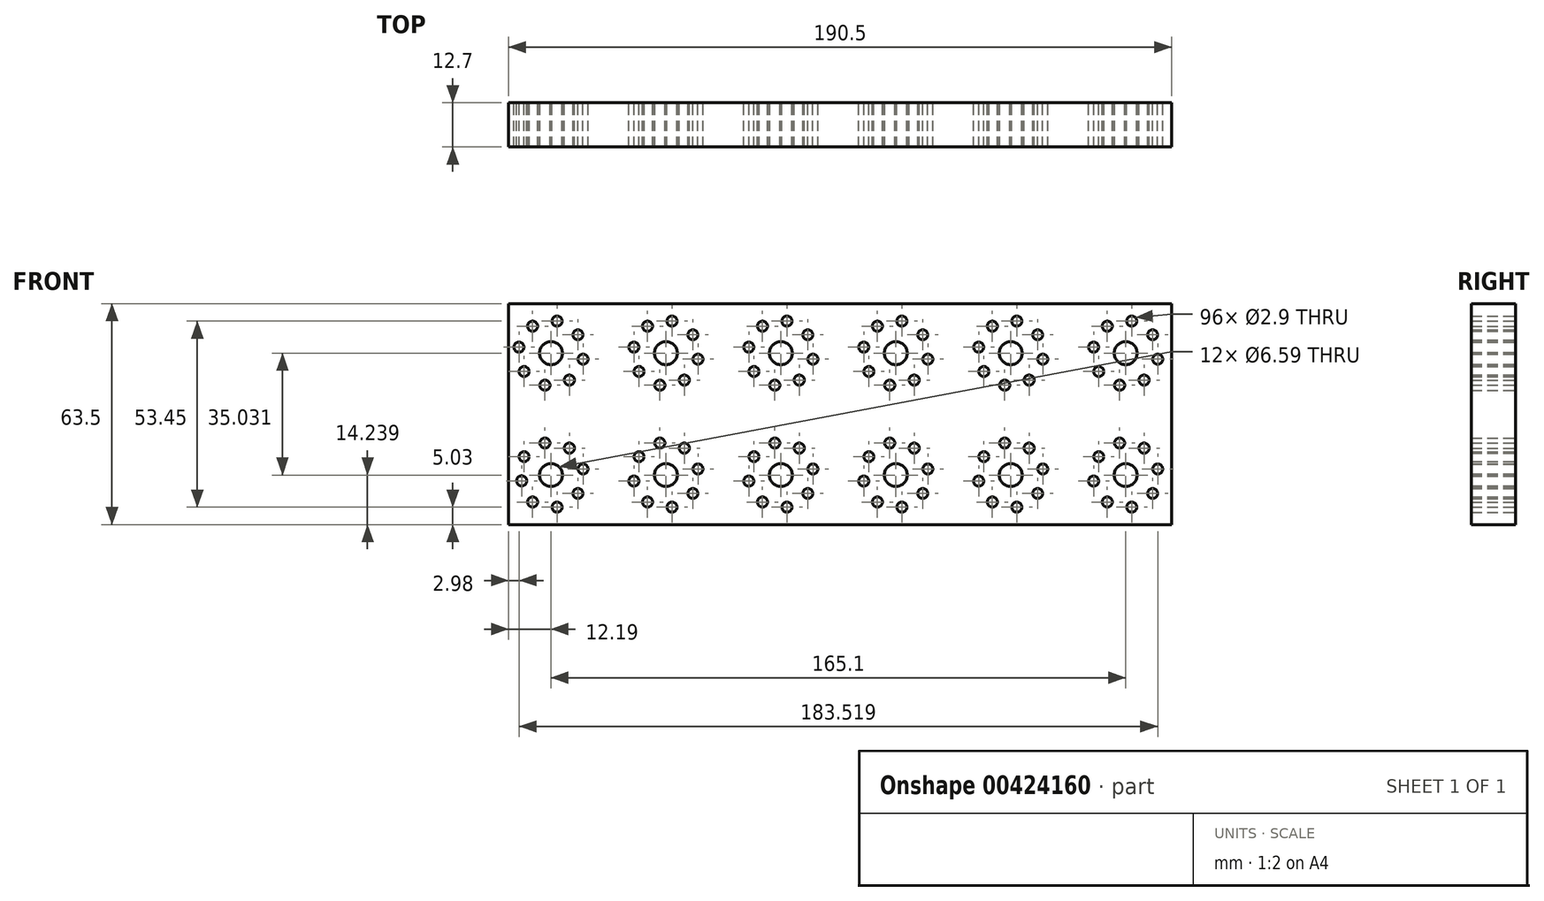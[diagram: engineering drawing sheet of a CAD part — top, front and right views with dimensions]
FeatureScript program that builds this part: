
annotation { "Feature Type Name" : "Feature", "Feature Type Description" : "" }
export const myFeature = defineFeature(function(context is Context, id is Id, definition is map)
    precondition{}
    {
        {
            var Q0;
            Q0=qCreatedBy(makeId("Front.planeOp"),FACE);
            var sketch = newSketch(context, id + "F0", { "sketchPlane" : qUnion([Q0])});
            skPoint(sketch, "E0.middle", {"position": v(0, 0) * mm});
            skCircle(sketch, "E1", {"center": v(-73.12, 32.93) * mm, "radius": 3.3 * mm});
            skCircle(sketch, "E2", {"center": v(-65.38, 38.21) * mm, "radius": 1.45 * mm});
            skCircle(sketch, "E3.1.0", {"center": v(-71.38, 42.14) * mm, "radius": 1.45 * mm});
            skCircle(sketch, "E3.2.0", {"center": v(-78.4, 40.67) * mm, "radius": 1.45 * mm});
            skCircle(sketch, "E3.3.0", {"center": v(-82.33, 34.67) * mm, "radius": 1.45 * mm});
            skCircle(sketch, "E3.4.0", {"center": v(-80.86, 27.65) * mm, "radius": 1.45 * mm});
            skCircle(sketch, "E3.5.0", {"center": v(-74.86, 23.72) * mm, "radius": 1.45 * mm});
            skCircle(sketch, "E3.6.0", {"center": v(-67.84, 25.19) * mm, "radius": 1.45 * mm});
            skCircle(sketch, "E3.7.0", {"center": v(-63.91, 31.2) * mm, "radius": 1.45 * mm});
            skCircle(sketch, "E4.1.0.0", {"center": v(-49.3, 34.67) * mm, "radius": 1.45 * mm});
            skCircle(sketch, "E4.1.0.1", {"center": v(-45.38, 40.67) * mm, "radius": 1.45 * mm});
            skCircle(sketch, "E4.1.0.2", {"center": v(-41.84, 23.72) * mm, "radius": 1.45 * mm});
            skCircle(sketch, "E4.1.0.3", {"center": v(-34.82, 25.19) * mm, "radius": 1.45 * mm});
            skPoint(sketch, "E4.1.0.4", {"position": v(-40.1, 32.93) * mm});
            skCircle(sketch, "E4.1.0.5", {"center": v(-30.9, 31.2) * mm, "radius": 1.45 * mm});
            skCircle(sketch, "E4.1.0.6", {"center": v(-32.36, 38.21) * mm, "radius": 1.45 * mm});
            skCircle(sketch, "E4.1.0.7", {"center": v(-38.36, 42.14) * mm, "radius": 1.45 * mm});
            skCircle(sketch, "E4.1.0.8", {"center": v(-47.84, 27.65) * mm, "radius": 1.45 * mm});
            skCircle(sketch, "E4.1.0.9", {"center": v(-40.1, 32.93) * mm, "radius": 3.3 * mm});
            skCircle(sketch, "E4.2.0.0", {"center": v(-16.29, 34.67) * mm, "radius": 1.45 * mm});
            skCircle(sketch, "E4.2.0.1", {"center": v(-12.36, 40.67) * mm, "radius": 1.45 * mm});
            skCircle(sketch, "E4.2.0.2", {"center": v(-8.82, 23.72) * mm, "radius": 1.45 * mm});
            skCircle(sketch, "E4.2.0.3", {"center": v(-1.8, 25.19) * mm, "radius": 1.45 * mm});
            skPoint(sketch, "E4.2.0.4", {"position": v(-7.08, 32.93) * mm});
            skCircle(sketch, "E4.2.0.5", {"center": v(2.13, 31.2) * mm, "radius": 1.45 * mm});
            skCircle(sketch, "E4.2.0.6", {"center": v(0.66, 38.21) * mm, "radius": 1.45 * mm});
            skCircle(sketch, "E4.2.0.7", {"center": v(-5.34, 42.14) * mm, "radius": 1.45 * mm});
            skCircle(sketch, "E4.2.0.8", {"center": v(-14.82, 27.65) * mm, "radius": 1.45 * mm});
            skCircle(sketch, "E4.2.0.9", {"center": v(-7.08, 32.93) * mm, "radius": 3.3 * mm});
            skCircle(sketch, "E4.3.0.0", {"center": v(16.73, 34.67) * mm, "radius": 1.45 * mm});
            skCircle(sketch, "E4.3.0.1", {"center": v(20.66, 40.67) * mm, "radius": 1.45 * mm});
            skCircle(sketch, "E4.3.0.2", {"center": v(24.2, 23.72) * mm, "radius": 1.45 * mm});
            skCircle(sketch, "E4.3.0.3", {"center": v(31.22, 25.19) * mm, "radius": 1.45 * mm});
            skPoint(sketch, "E4.3.0.4", {"position": v(25.94, 32.93) * mm});
            skCircle(sketch, "E4.3.0.5", {"center": v(35.15, 31.2) * mm, "radius": 1.45 * mm});
            skCircle(sketch, "E4.3.0.6", {"center": v(33.68, 38.21) * mm, "radius": 1.45 * mm});
            skCircle(sketch, "E4.3.0.7", {"center": v(27.68, 42.14) * mm, "radius": 1.45 * mm});
            skCircle(sketch, "E4.3.0.8", {"center": v(18.2, 27.65) * mm, "radius": 1.45 * mm});
            skCircle(sketch, "E4.3.0.9", {"center": v(25.94, 32.93) * mm, "radius": 3.3 * mm});
            skCircle(sketch, "E4.4.0.0", {"center": v(49.75, 34.67) * mm, "radius": 1.45 * mm});
            skCircle(sketch, "E4.4.0.1", {"center": v(53.68, 40.67) * mm, "radius": 1.45 * mm});
            skCircle(sketch, "E4.4.0.2", {"center": v(57.22, 23.72) * mm, "radius": 1.45 * mm});
            skCircle(sketch, "E4.4.0.3", {"center": v(64.24, 25.19) * mm, "radius": 1.45 * mm});
            skPoint(sketch, "E4.4.0.4", {"position": v(58.96, 32.93) * mm});
            skCircle(sketch, "E4.4.0.5", {"center": v(68.17, 31.2) * mm, "radius": 1.45 * mm});
            skCircle(sketch, "E4.4.0.6", {"center": v(66.7, 38.21) * mm, "radius": 1.45 * mm});
            skCircle(sketch, "E4.4.0.7", {"center": v(60.7, 42.14) * mm, "radius": 1.45 * mm});
            skCircle(sketch, "E4.4.0.8", {"center": v(51.22, 27.65) * mm, "radius": 1.45 * mm});
            skCircle(sketch, "E4.4.0.9", {"center": v(58.96, 32.93) * mm, "radius": 3.3 * mm});
            skCircle(sketch, "E4.5.0.0", {"center": v(82.77, 34.67) * mm, "radius": 1.45 * mm});
            skCircle(sketch, "E4.5.0.1", {"center": v(86.7, 40.67) * mm, "radius": 1.45 * mm});
            skCircle(sketch, "E4.5.0.2", {"center": v(90.24, 23.72) * mm, "radius": 1.45 * mm});
            skCircle(sketch, "E4.5.0.3", {"center": v(97.26, 25.19) * mm, "radius": 1.45 * mm});
            skPoint(sketch, "E4.5.0.4", {"position": v(91.98, 32.93) * mm});
            skCircle(sketch, "E4.5.0.5", {"center": v(101.19, 31.2) * mm, "radius": 1.45 * mm});
            skCircle(sketch, "E4.5.0.6", {"center": v(99.72, 38.21) * mm, "radius": 1.45 * mm});
            skCircle(sketch, "E4.5.0.7", {"center": v(93.72, 42.14) * mm, "radius": 1.45 * mm});
            skCircle(sketch, "E4.5.0.8", {"center": v(84.24, 27.65) * mm, "radius": 1.45 * mm});
            skCircle(sketch, "E4.5.0.9", {"center": v(91.98, 32.93) * mm, "radius": 3.3 * mm});
            skLineSegment(sketch, "E4.direction1", {"start": v(-80.86, 27.65) * mm, "end": v(-47.84, 27.65) * mm, "construction": true});
            skLineSegment(sketch, "E5.bottom", {"start": v(-85.3, 47.16) * mm, "end": v(105.2, 47.16) * mm});
            skLineSegment(sketch, "E5.top", {"start": v(-85.3, -16.34) * mm, "end": v(105.2, -16.34) * mm});
            skLineSegment(sketch, "E5.left", {"start": v(-85.3, 47.16) * mm, "end": v(-85.3, -16.34) * mm});
            skLineSegment(sketch, "E5.right", {"start": v(105.2, 47.16) * mm, "end": v(105.2, -16.34) * mm});
            skCircle(sketch, "E6.MirrorC", {"center": v(-80.86, 3.18) * mm, "radius": 1.45 * mm});
            skCircle(sketch, "E7.MirrorC", {"center": v(-47.84, 3.18) * mm, "radius": 1.45 * mm});
            skCircle(sketch, "E8.MirrorC", {"center": v(-8.82, 7.1) * mm, "radius": 1.45 * mm});
            skCircle(sketch, "E9.MirrorC", {"center": v(-71.38, -11.31) * mm, "radius": 1.45 * mm});
            skCircle(sketch, "E10.MirrorC", {"center": v(-65.38, -7.38) * mm, "radius": 1.45 * mm});
            skCircle(sketch, "E11.MirrorC", {"center": v(-78.4, -9.84) * mm, "radius": 1.45 * mm});
            skCircle(sketch, "E12.MirrorC", {"center": v(-49.3, -3.84) * mm, "radius": 1.45 * mm});
            skCircle(sketch, "E13.MirrorC", {"center": v(-45.38, -9.84) * mm, "radius": 1.45 * mm});
            skCircle(sketch, "E14.MirrorC", {"center": v(27.68, -11.31) * mm, "radius": 1.45 * mm});
            skCircle(sketch, "E15.MirrorC", {"center": v(51.22, 3.18) * mm, "radius": 1.45 * mm});
            skCircle(sketch, "E16.MirrorC", {"center": v(35.15, -0.36) * mm, "radius": 1.45 * mm});
            skCircle(sketch, "E17.MirrorC", {"center": v(0.66, -7.38) * mm, "radius": 1.45 * mm});
            skCircle(sketch, "E18.MirrorC", {"center": v(90.24, 7.1) * mm, "radius": 1.45 * mm});
            skCircle(sketch, "E19.MirrorC", {"center": v(57.22, 7.1) * mm, "radius": 1.45 * mm});
            skCircle(sketch, "E20.MirrorC", {"center": v(64.24, 5.64) * mm, "radius": 1.45 * mm});
            skCircle(sketch, "E21.MirrorC", {"center": v(-34.82, 5.64) * mm, "radius": 1.45 * mm});
            skCircle(sketch, "E22.MirrorC", {"center": v(16.73, -3.84) * mm, "radius": 1.45 * mm});
            skCircle(sketch, "E23.MirrorC", {"center": v(2.13, -0.36) * mm, "radius": 1.45 * mm});
            skCircle(sketch, "E24.MirrorC", {"center": v(82.77, -3.84) * mm, "radius": 1.45 * mm});
            skCircle(sketch, "E25.MirrorC", {"center": v(84.24, 3.18) * mm, "radius": 1.45 * mm});
            skCircle(sketch, "E26.MirrorC", {"center": v(-74.86, 7.1) * mm, "radius": 1.45 * mm});
            skCircle(sketch, "E27.MirrorC", {"center": v(24.2, 7.1) * mm, "radius": 1.45 * mm});
            skCircle(sketch, "E28.MirrorC", {"center": v(49.75, -3.84) * mm, "radius": 1.45 * mm});
            skCircle(sketch, "E29.MirrorC", {"center": v(-16.29, -3.84) * mm, "radius": 1.45 * mm});
            skCircle(sketch, "E30.MirrorC", {"center": v(-63.91, -0.36) * mm, "radius": 1.45 * mm});
            skCircle(sketch, "E31.MirrorC", {"center": v(-12.36, -9.84) * mm, "radius": 1.45 * mm});
            skCircle(sketch, "E32.MirrorC", {"center": v(31.22, 5.64) * mm, "radius": 1.45 * mm});
            skCircle(sketch, "E33.MirrorC", {"center": v(-41.84, 7.1) * mm, "radius": 1.45 * mm});
            skCircle(sketch, "E34.MirrorC", {"center": v(53.68, -9.84) * mm, "radius": 1.45 * mm});
            skCircle(sketch, "E35.MirrorC", {"center": v(86.7, -9.84) * mm, "radius": 1.45 * mm});
            skCircle(sketch, "E36.MirrorC", {"center": v(60.7, -11.31) * mm, "radius": 1.45 * mm});
            skCircle(sketch, "E37.MirrorC", {"center": v(-67.84, 5.64) * mm, "radius": 1.45 * mm});
            skCircle(sketch, "E38.MirrorC", {"center": v(-14.82, 3.18) * mm, "radius": 1.45 * mm});
            skCircle(sketch, "E39.MirrorC", {"center": v(20.66, -9.84) * mm, "radius": 1.45 * mm});
            skCircle(sketch, "E40.MirrorC", {"center": v(-1.8, 5.64) * mm, "radius": 1.45 * mm});
            skCircle(sketch, "E41.MirrorC", {"center": v(93.72, -11.31) * mm, "radius": 1.45 * mm});
            skCircle(sketch, "E42.MirrorC", {"center": v(18.2, 3.18) * mm, "radius": 1.45 * mm});
            skCircle(sketch, "E43.MirrorC", {"center": v(68.17, -0.36) * mm, "radius": 1.45 * mm});
            skCircle(sketch, "E44.MirrorC", {"center": v(97.26, 5.64) * mm, "radius": 1.45 * mm});
            skCircle(sketch, "E45.MirrorC", {"center": v(99.72, -7.38) * mm, "radius": 1.45 * mm});
            skCircle(sketch, "E46.MirrorC", {"center": v(-5.34, -11.31) * mm, "radius": 1.45 * mm});
            skCircle(sketch, "E47.MirrorC", {"center": v(-30.9, -0.36) * mm, "radius": 1.45 * mm});
            skCircle(sketch, "E48.MirrorC", {"center": v(-32.36, -7.38) * mm, "radius": 1.45 * mm});
            skCircle(sketch, "E49.MirrorC", {"center": v(66.7, -7.38) * mm, "radius": 1.45 * mm});
            skCircle(sketch, "E50.MirrorC", {"center": v(33.68, -7.38) * mm, "radius": 1.45 * mm});
            skCircle(sketch, "E51.MirrorC", {"center": v(-38.36, -11.31) * mm, "radius": 1.45 * mm});
            skCircle(sketch, "E52.MirrorC", {"center": v(101.19, -0.36) * mm, "radius": 1.45 * mm});
            skPoint(sketch, "E53.MirrorP", {"position": v(-40.1, -2.1) * mm});
            skPoint(sketch, "E54.MirrorP", {"position": v(-73.12, -2.1) * mm});
            skLineSegment(sketch, "E55.MirrorCS", {"start": v(-80.86, 3.18) * mm, "end": v(-47.84, 3.18) * mm, "construction": true});
            skPoint(sketch, "E56.MirrorP", {"position": v(91.98, -2.1) * mm});
            skCircle(sketch, "E57.MirrorC", {"center": v(91.98, -2.1) * mm, "radius": 3.3 * mm});
            skPoint(sketch, "E58.MirrorP", {"position": v(25.94, -2.1) * mm});
            skCircle(sketch, "E59.MirrorC", {"center": v(-73.12, -2.1) * mm, "radius": 3.3 * mm});
            skCircle(sketch, "E60.MirrorC", {"center": v(-7.08, -2.1) * mm, "radius": 3.3 * mm});
            skCircle(sketch, "E61.MirrorC", {"center": v(58.96, -2.1) * mm, "radius": 3.3 * mm});
            skCircle(sketch, "E62.MirrorC", {"center": v(25.94, -2.1) * mm, "radius": 3.3 * mm});
            skCircle(sketch, "E63.MirrorC", {"center": v(-40.1, -2.1) * mm, "radius": 3.3 * mm});
            skCircle(sketch, "E64.MirrorC", {"center": v(-81.54, -3.77) * mm, "radius": 1.45 * mm});
            skSolve(sketch);
        }
        {
            var Q0;
            Q0=makeQuery(id+"F0.imprint","IMPRINT",FACE,{"disambiguationData":[TD([[makeQuery(id+"F0.imprint","IMPRINT",EDGE,{"derivedFrom":sQuery(id+"F0.wireOp",EDGE,"E1")}),-1.0]])]});
            extrude(context, id + "F1", {"entities" : qUnion([Q0]), "depth" : 12.7 * mm});
        }
    });
